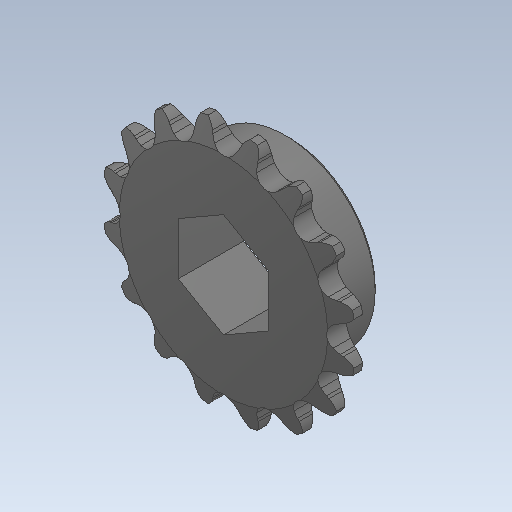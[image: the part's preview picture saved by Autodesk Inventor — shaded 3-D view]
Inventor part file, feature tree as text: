
AUTODESK INVENTOR PART (.ipt)
format: ipt  version: 2020 (Build 240168000, 168)  size: 485,376 bytes
history: native  units: in
note: dims shown in document units (in); Inventor stores cm internally (conversion verified against a paired STEP export)
features: chamfer x1
ambient origin geometry x8: Origin, YZ Plane, XZ Plane, XY Plane, X Axis, Y Axis, Z Axis, Center Point
bodies: Solid1 (feature_tree)
feature tree (1):
  chamfer  "Chamfer2"  [1 undecoded]
note: 1 required parameter value undecoded (feature->parameter linkage not recoverable at this tier; creation-order binding heuristic only, values carry confidence <= 0.55)
